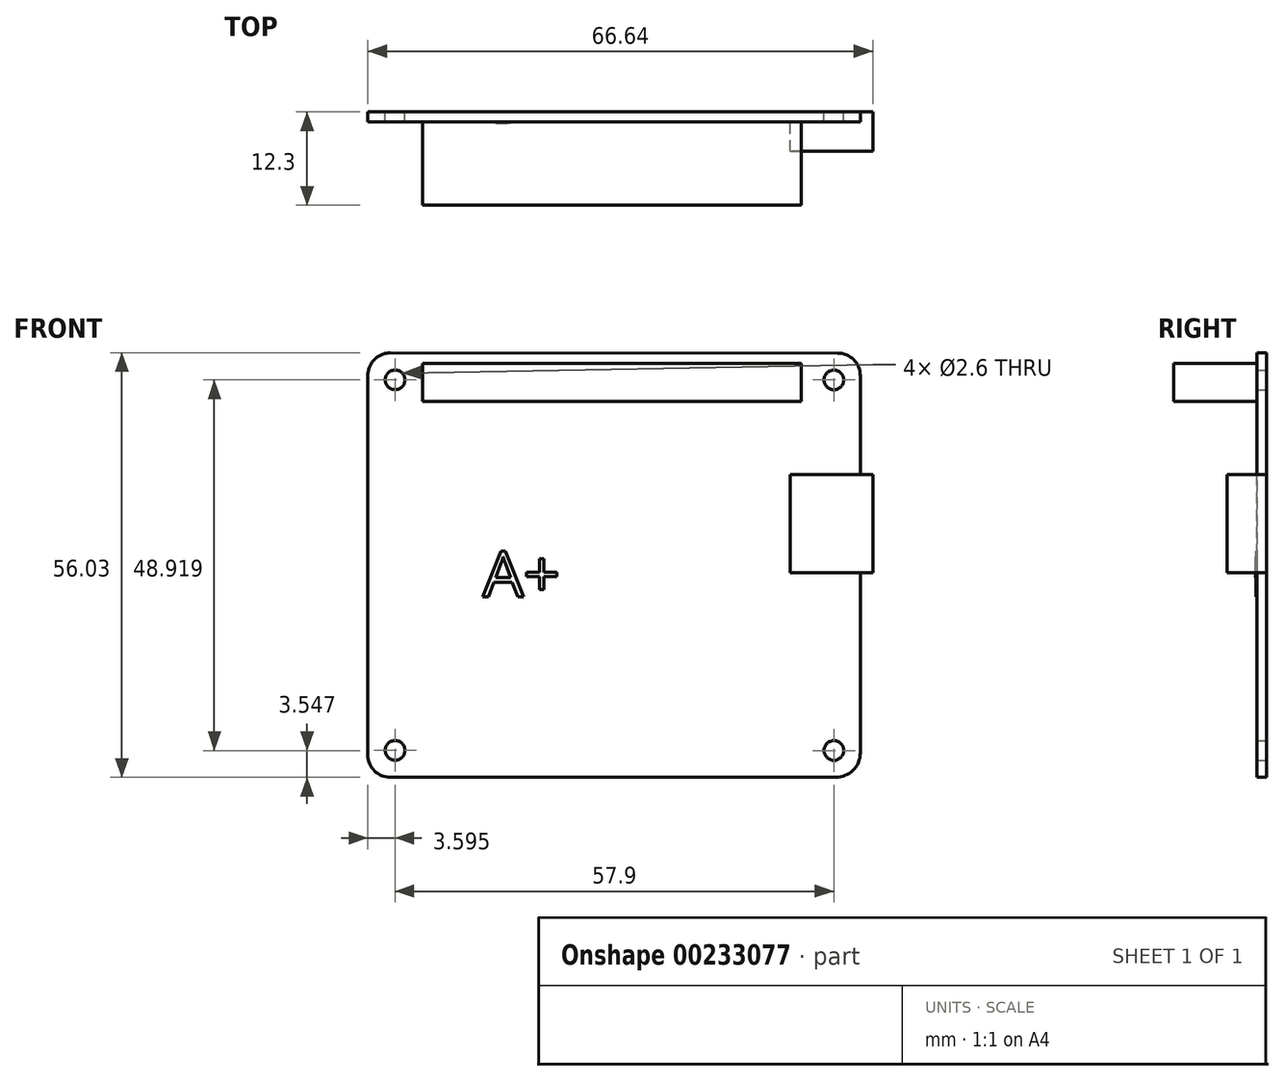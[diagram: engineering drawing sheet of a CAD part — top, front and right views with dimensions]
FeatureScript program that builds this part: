
annotation { "Feature Type Name" : "Feature", "Feature Type Description" : "" }
export const myFeature = defineFeature(function(context is Context, id is Id, definition is map)
    precondition{}
    {
        {
            var Q0;
            Q0=qCreatedBy(makeId("Front.planeOp"),FACE);
            var sketch = newSketch(context, id + "F0", { "sketchPlane" : qUnion([Q0])});
            skLineSegment(sketch, "E0", {"start": v(31.85, 21.56) * mm, "end": v(31.85, -28.2) * mm});
            skLineSegment(sketch, "E1", {"start": v(28.6, -31.44) * mm, "end": v(-30.15, -31.44) * mm});
            skLineSegment(sketch, "E2", {"start": v(28.85, 24.56) * mm, "end": v(-30.15, 24.59) * mm});
            skLineSegment(sketch, "E3", {"start": v(31.85, 24.56) * mm, "end": v(31.85, 21) * mm, "construction": true});
            skPoint(sketch, "E4.visualSharp", {"position": v(31.85, 24.56) * mm});
            skArc(sketch, "E4.filletArc", {"start": v(-30.15, 24.59) * mm, "mid": v(-32.28, 23.7) * mm, "end": v(-33.15, 21.59) * mm});
            skPoint(sketch, "E5.visualSharp", {"position": v(-33.15, -31.44) * mm});
            skArc(sketch, "E5.filletArc", {"start": v(-33.15, -28.44) * mm, "mid": v(-32.28, -30.56) * mm, "end": v(-30.15, -31.44) * mm});
            skPoint(sketch, "E6.visualSharp", {"position": v(31.85, -31.44) * mm});
            skArc(sketch, "E6.filletArc", {"start": v(28.6, -31.44) * mm, "mid": v(30.9, -30.5) * mm, "end": v(31.85, -28.2) * mm});
            skArc(sketch, "E7.filletArc", {"start": v(31.85, 21.56) * mm, "mid": v(30.97, 23.68) * mm, "end": v(28.85, 24.56) * mm});
            skLineSegment(sketch, "E8", {"start": v(31.85, 21) * mm, "end": v(28.35, 21) * mm});
            skCircle(sketch, "E9", {"center": v(28.35, 21) * mm, "radius": 1.3 * mm});
            skLineSegment(sketch, "E10", {"start": v(31.85, -31.44) * mm, "end": v(31.85, -28.2) * mm, "construction": true});
            skLineSegment(sketch, "E11", {"start": v(28.35, 21) * mm, "end": v(28.35, -44.74) * mm, "construction": true});
            skLineSegment(sketch, "E12", {"start": v(31.85, -28.2) * mm, "end": v(28.35, -28.2) * mm, "construction": true});
            skLineSegment(sketch, "E13", {"start": v(-33.15, -31.44) * mm, "end": v(-29.55, -31.44) * mm, "construction": true});
            skLineSegment(sketch, "E14", {"start": v(-21.97, 24.58) * mm, "end": v(-21.97, 18.18) * mm, "construction": true});
            skLineSegment(sketch, "E15", {"start": v(-32.85, 18.18) * mm, "end": v(-25.95, 18.18) * mm, "construction": true});
            skLineSegment(sketch, "E16", {"start": v(-25.95, 18.18) * mm, "end": v(-25.95, 23.18) * mm});
            skLineSegment(sketch, "E17", {"start": v(-25.95, 18.18) * mm, "end": v(24.05, 18.18) * mm});
            skLineSegment(sketch, "E18", {"start": v(24.05, 18.18) * mm, "end": v(24.05, 23.18) * mm});
            skLineSegment(sketch, "E19", {"start": v(-25.95, 23.18) * mm, "end": v(24.05, 23.18) * mm});
            skCircle(sketch, "E20", {"center": v(28.35, -27.9) * mm, "radius": 1.3 * mm});
            skCircle(sketch, "E21", {"center": v(-29.55, -27.87) * mm, "radius": 1.3 * mm});
            skLineSegment(sketch, "E22", {"start": v(-30.15, 24.59) * mm, "end": v(-30.15, 21.03) * mm, "construction": true});
            skLineSegment(sketch, "E23", {"start": v(-29.55, -31.44) * mm, "end": v(-29.55, 27.6) * mm, "construction": true});
            skLineSegment(sketch, "E24", {"start": v(-30.15, 21.03) * mm, "end": v(-29.27, 21.03) * mm, "construction": true});
            skCircle(sketch, "E25", {"center": v(-29.55, 21.03) * mm, "radius": 1.3 * mm});
            skLineSegment(sketch, "E26", {"start": v(-33.15, 21.59) * mm, "end": v(-33.15, -28.44) * mm});
            skLineSegment(sketch, "E27", {"start": v(31.85, 24.56) * mm, "end": v(31.85, 8.56) * mm, "construction": true});
            skLineSegment(sketch, "E28", {"start": v(31.85, 8.56) * mm, "end": v(22.6, 8.56) * mm, "construction": true});
            skLineSegment(sketch, "E29", {"start": v(22.6, 8.56) * mm, "end": v(33.49, 8.56) * mm});
            skLineSegment(sketch, "E30", {"start": v(33.49, 8.56) * mm, "end": v(33.49, -4.44) * mm});
            skLineSegment(sketch, "E31", {"start": v(33.49, -4.44) * mm, "end": v(22.6, -4.44) * mm});
            skLineSegment(sketch, "E32", {"start": v(22.6, -4.44) * mm, "end": v(22.6, 8.56) * mm});
            skText(sketch, "E33", { "text": "A+", "fontName": "OpenSans-Regular.ttf"});
            skLineSegment(sketch, "E34", {"start": v(31.85, 24.56) * mm, "end": v(31.85, -3.32) * mm, "construction": true});
            const initialGuessF0  = {"E33": [-0.01796, -0.0076, 1, 0, 0.00608]};
            skSetInitialGuess(sketch, initialGuessF0);
            skSolve(sketch);
        }
        {
            var Q0;
            Q0=makeQuery(id+"F0.imprint","IMPRINT",FACE,{"disambiguationData":[TD([[makeQuery(id+"F0.imprint","IMPRINT",EDGE,{"derivedFrom":sQuery(id+"F0.wireOp",EDGE,"E1")}),-1.0]])]});
            extrude(context, id + "F1", {"entities" : qUnion([Q0]), "depth" : 1.3 * mm});
        }
        {
            var Q0;
            Q0=makeQuery(id+"F0.imprint","IMPRINT",FACE,{"disambiguationData":[TD([[makeQuery(id+"F0.imprint","IMPRINT",EDGE,{"derivedFrom":sQuery(id+"F0.wireOp",EDGE,"E16")}),-1.0]])]});
            extrude(context, id + "F2", {"entities" : qUnion([Q0]), "operationType" : NewBodyOperationType.ADD, "depth" : 12.3 * mm});
        }
        {
            var Q0;
            {var subQ5=sQuery(id+"F0.wireOp",EDGE,"E32");Q0=makeQuery(id+"F0.imprint","IMPRINT",FACE,{"disambiguationData":[TD([[makeQuery(id+"F0.imprint","IMPRINT",EDGE,{"derivedFrom":subQ5}),-1.0]])]});}
            var Q1;
            {var subQ5=sQuery(id+"F0.wireOp",EDGE,"E30");Q1=makeQuery(id+"F0.imprint","IMPRINT",FACE,{"disambiguationData":[TD([[makeQuery(id+"F0.imprint","IMPRINT",EDGE,{"derivedFrom":subQ5}),-1.0]])]});}
            extrude(context, id + "F3", {"entities" : qUnion([Q0, Q1]), "operationType" : NewBodyOperationType.ADD, "depth" : 5.2 * mm});
        }
        {
            var Q0;
            Q0=makeQuery(id+"F0.imprint","IMPRINT",FACE,{"disambiguationData":[TD([[makeQuery(id+"F0.imprint","IMPRINT",EDGE,{"derivedFrom":sQuery(id+"F0.wireOp",EDGE,"E33.sketch_text.stroke-0")}),-1.0]])]});
            var Q1;
            Q1=makeQuery(id+"F0.imprint","IMPRINT",FACE,{"disambiguationData":[TD([[makeQuery(id+"F0.imprint","IMPRINT",EDGE,{"derivedFrom":sQuery(id+"F0.wireOp",EDGE,"E33.sketch_text.stroke-8")}),1.0]])]});
            var Q2;
            Q2=makeQuery(id+"F0.imprint","IMPRINT",FACE,{"disambiguationData":[TD([[makeQuery(id+"F0.imprint","IMPRINT",EDGE,{"derivedFrom":sQuery(id+"F0.wireOp",EDGE,"E33.sketch_text.stroke-13")}),-1.0]])]});
            extrude(context, id + "F4", {"entities" : qUnion([Q0, Q1, Q2]), "operationType" : NewBodyOperationType.ADD, "depth" : 1.4 * mm});
        }
        {
            var Q0;
            Q0=makeQuery(id+"F0.imprint","IMPRINT",FACE,{"disambiguationData":[TD([[makeQuery(id+"F0.imprint","IMPRINT",EDGE,{"derivedFrom":sQuery(id+"F0.wireOp",EDGE,"E33.sketch_text.stroke-8")}),1.0]])]});
            extrude(context, id + "F5", {"entities" : qUnion([Q0]), "operationType" : NewBodyOperationType.ADD, "depth" : 1.5 * mm});
        }
    });
